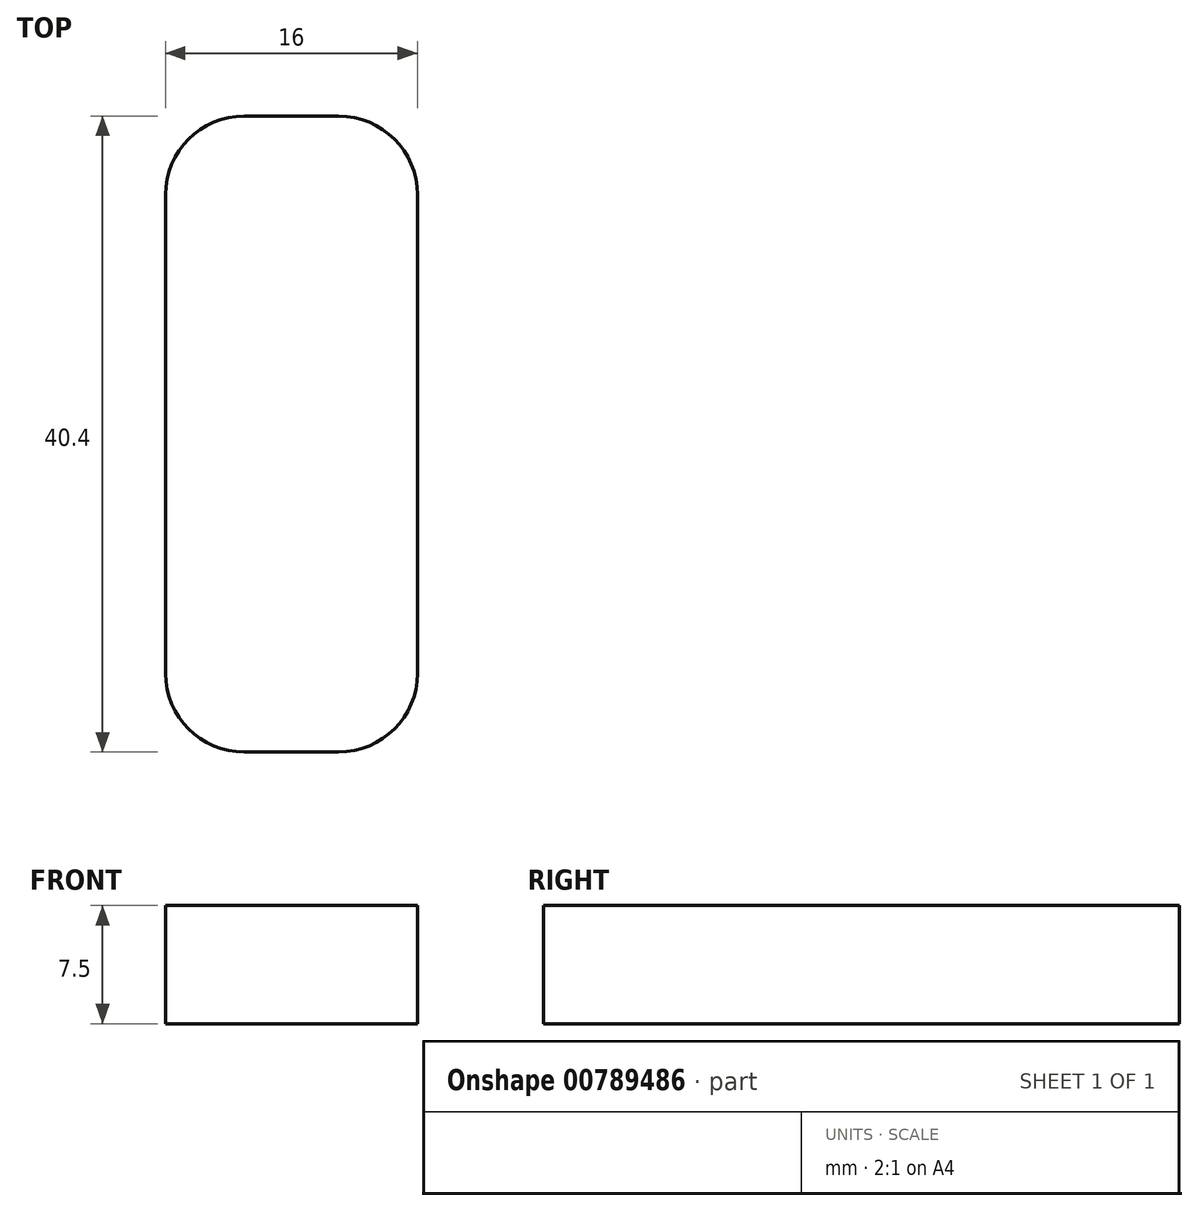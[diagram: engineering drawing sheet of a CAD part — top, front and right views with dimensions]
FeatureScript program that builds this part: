
annotation { "Feature Type Name" : "Feature", "Feature Type Description" : "" }
export const myFeature = defineFeature(function(context is Context, id is Id, definition is map)
    precondition{}
    {
        {
            var Q0;
            Q0=qCreatedBy(makeId("Top.planeOp"),FACE);
            var sketch = newSketch(context, id + "F0", { "sketchPlane" : qUnion([Q0])});
            skLineSegment(sketch, "E0.bottom", {"start": v(-8, -20.2) * mm, "end": v(8, -20.2) * mm});
            skLineSegment(sketch, "E0.top", {"start": v(-8, 20.2) * mm, "end": v(8, 20.2) * mm});
            skLineSegment(sketch, "E0.left", {"start": v(-8, -20.2) * mm, "end": v(-8, 20.2) * mm});
            skLineSegment(sketch, "E0.right", {"start": v(8, -20.2) * mm, "end": v(8, 20.2) * mm});
            skPoint(sketch, "E0.middle", {"position": v(0, 0) * mm});
            skSolve(sketch);
        }
        {
            var Q0;
            Q0=makeQuery(id+"F0.imprint","IMPRINT",FACE,{"disambiguationData":[TD([[makeQuery(id+"F0.imprint","IMPRINT",EDGE,{"derivedFrom":sQuery(id+"F0.wireOp",EDGE,"E0.bottom")}),1.0]])]});
            extrude(context, id + "F1", {"entities" : qUnion([Q0]), "depth" : 7.5 * mm, "offsetDistance" : 25 * mm});
        }
        {
            var Q0;
            Q0=makeQuery(id+"F1.opExtrude","SWEPT_EDGE",EDGE,{"disambiguationData":[OSD([sQuery(id+"F0.wireOp",EDGE,"E0.bottom"),sQuery(id+"F0.wireOp",EDGE,"E0.right")])]});
            var Q1;
            Q1=makeQuery(id+"F1.opExtrude","SWEPT_EDGE",EDGE,{"disambiguationData":[OSD([sQuery(id+"F0.wireOp",EDGE,"E0.bottom"),sQuery(id+"F0.wireOp",EDGE,"E0.left")])]});
            var Q2;
            Q2=makeQuery(id+"F1.opExtrude","SWEPT_EDGE",EDGE,{"disambiguationData":[OSD([sQuery(id+"F0.wireOp",EDGE,"E0.top"),sQuery(id+"F0.wireOp",EDGE,"E0.right")])]});
            var Q3;
            Q3=makeQuery(id+"F1.opExtrude","SWEPT_EDGE",EDGE,{"disambiguationData":[OSD([sQuery(id+"F0.wireOp",EDGE,"E0.top"),sQuery(id+"F0.wireOp",EDGE,"E0.left")])]});
            fillet(context, id + "F2", {"entities" : qUnion([Q0, Q1, Q2, Q3]), "radius" : 5 * mm, "tangentPropagation" : true, "allowEdgeOverflow" : false});
        }
    });
